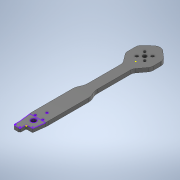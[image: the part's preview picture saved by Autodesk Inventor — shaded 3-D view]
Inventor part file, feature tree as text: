
AUTODESK INVENTOR PART (.ipt)
format: ipt  version: 2020 (Build 240168000, 168)  size: 303,104 bytes
history: native  units: in
note: dims shown in document units (in); Inventor stores cm internally (conversion verified against a paired STEP export)
features: extrude x9, sketch x4, fillet x2
ambient origin geometry x8: Origin, YZ Plane, XZ Plane, XY Plane, X Axis, Y Axis, Z Axis, Center Point
bodies: Body1 (feature_tree)
feature tree (15):
  extrude  "Extrusion1"  Depth=0.2362in
  sketch  "Sketch4"  dims[d7=0.4724in d9=7.0in d10=6.8898in d11=6.8898in]
  extrude  "Extrusion2"  Depth=7.0in
  fillet  "Fillet2"  Radius=6.8898in
  fillet  "Fillet3"  Radius=6.8898in
  sketch  "Sketch7"  dims[d14=0.9835in d15=0.9835in d16=0.9835in d17=0.1181in d18=0.0in d20=0.3937in d21=0.7874in d22=0.2362in d23=0.0in d24=0.2362in d25=0.0in d26=0.2362in d27=0.0in d28=0.2362in d29=0.0in d30=0.2362in d31=0.0in d32=0.2362in d33=0.0in d34=0.2362in d35=0.0in]
  extrude  "Extrusion3"  Depth=0.2992in
  extrude  "Extrusion4"  Depth=0.2362in
  extrude  "Extrusion5"  Depth=0.2362in
  extrude  "Extrusion6"  Depth=0.1181in TaperAngle=0.0deg
  extrude  "Extrusion7"  Depth=0.3937in
  extrude  "Extrusion8"  Depth=0.7874in
  extrude  "Extrusion9"  Depth=0.2362in TaperAngle=0.0deg
  sketch  "Sketch3"  dims[d2=0.2362in d3=0.0in d4=0.8352in]
  sketch  "Sketch5"  dims[d12=0.2992in d13=0.2992in]
